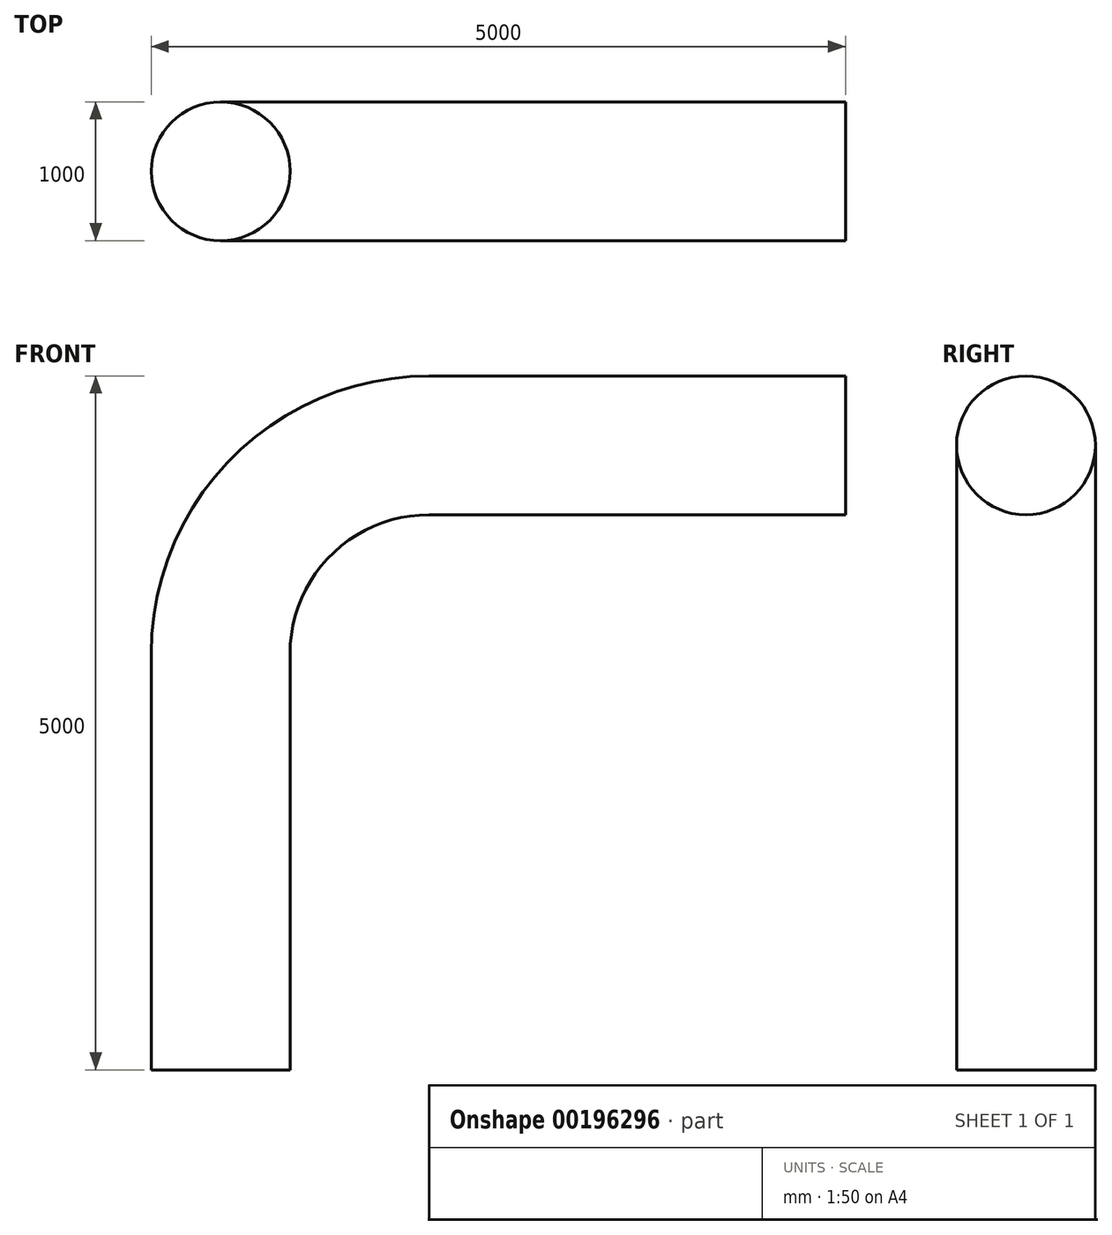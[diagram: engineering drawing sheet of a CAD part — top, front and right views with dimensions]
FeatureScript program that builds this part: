
annotation { "Feature Type Name" : "Feature", "Feature Type Description" : "" }
export const myFeature = defineFeature(function(context is Context, id is Id, definition is map)
    precondition{}
    {
        {
            var Q0;
            Q0=qCreatedBy(makeId("Front.planeOp"),FACE);
            var sketch = newSketch(context, id + "F0", { "sketchPlane" : qUnion([Q0])});
            skLineSegment(sketch, "E0", {"start": v(0, 0) * mm, "end": v(0, 3000) * mm});
            skArc(sketch, "E1", {"start": v(1500, 4500) * mm, "mid": v(439.34, 4060.66) * mm, "end": v(0, 3000) * mm});
            skLineSegment(sketch, "E2", {"start": v(1500, 4500) * mm, "end": v(4500, 4500) * mm});
            skSolve(sketch);
        }
        {
            var Q0;
            Q0=qCreatedBy(makeId("Top.planeOp"),FACE);
            var sketch = newSketch(context, id + "F1", { "sketchPlane" : qUnion([Q0])});
            skCircle(sketch, "E3", {"center": v(0, 0) * mm, "radius": 500 * mm});
            skSolve(sketch);
        }
        {
            var Q0;
            Q0=makeQuery(id+"F1.imprint","IMPRINT",FACE,{"disambiguationData":[TD([[makeQuery(id+"F1.imprint","IMPRINT",EDGE,{"derivedFrom":sQuery(id+"F1.wireOp",EDGE,"E3")}),1.0]])]});
            var Q1;
            Q1=sQuery(id+"F0.wireOp",EDGE,"E1");
            var Q2;
            Q2=sQuery(id+"F0.wireOp",EDGE,"E2");
            var Q3;
            Q3=sQuery(id+"F0.wireOp",EDGE,"E0");
            sweep(context, id + "F2", {"profiles" : qUnion([Q0]), "path" : qUnion([Q1, Q2, Q3])});
        }
    });
